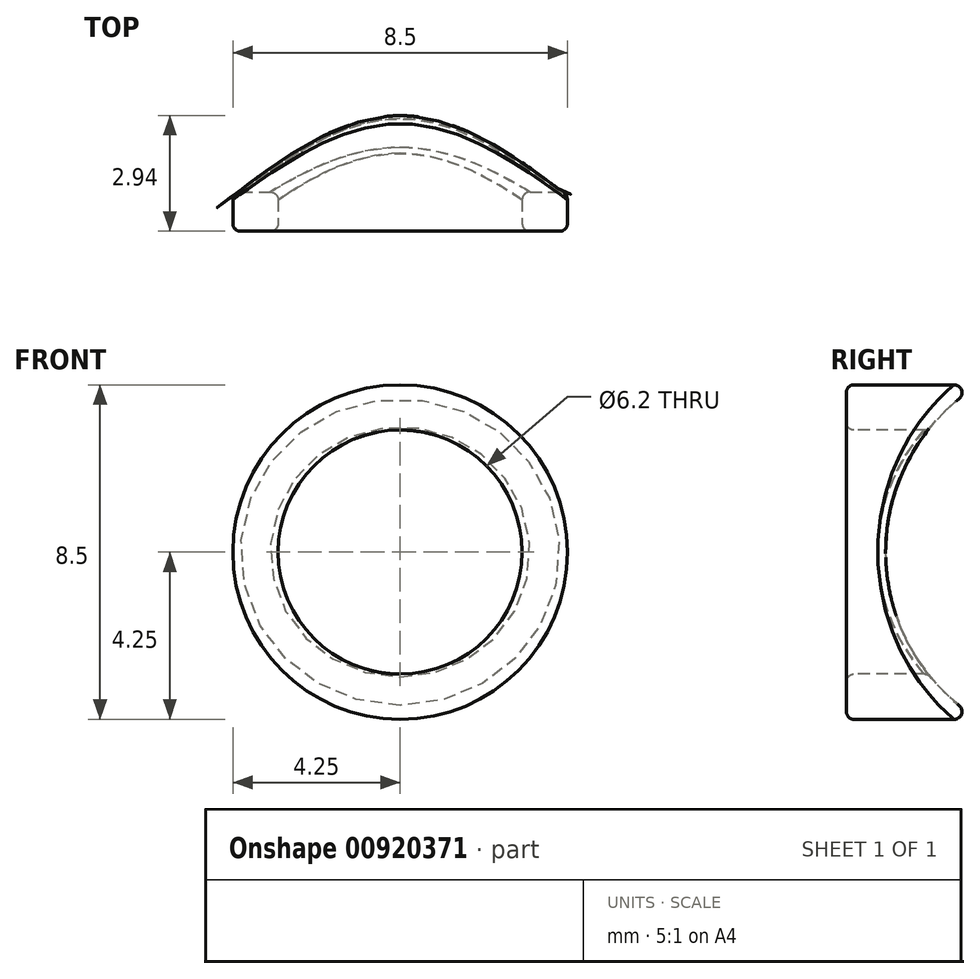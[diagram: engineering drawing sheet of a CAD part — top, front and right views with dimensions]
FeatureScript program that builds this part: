
annotation { "Feature Type Name" : "Feature", "Feature Type Description" : "" }
export const myFeature = defineFeature(function(context is Context, id is Id, definition is map)
    precondition{}
    {
        {
            var Q0;
            Q0=qCreatedBy(makeId("Front.planeOp"),FACE);
            var sketch = newSketch(context, id + "F0", { "sketchPlane" : qUnion([Q0])});
            skCircle(sketch, "E0", {"center": v(0, 0) * mm, "radius": 3.1 * mm});
            skCircle(sketch, "E1", {"center": v(0, 0) * mm, "radius": 4.25 * mm});
            skLineSegment(sketch, "E2", {"start": v(-9, 0) * mm, "end": v(9, 0) * mm, "construction": true});
            skCircle(sketch, "E3", {"center": v(0, 0) * mm, "radius": 9 * mm, "construction": true});
            skLineSegment(sketch, "E4", {"start": v(0, 9) * mm, "end": v(0, -9) * mm, "construction": true});
            skSolve(sketch);
        }
        {
            var Q0;
            Q0 = qSketchRegion(id + "F0", true);
            extrude(context, id + "F1", {"entities" : qUnion([Q0]), "oppositeDirection" : true, "depth" : 5 * mm, "offsetDistance" : 25 * mm});
        }
        {
            var Q0;
            Q0=qCreatedBy(makeId("Right.planeOp"),FACE);
            var sketch = newSketch(context, id + "F2", { "sketchPlane" : qUnion([Q0])});
            skLineSegment(sketch, "E5", {"start": v(0, 0) * mm, "end": v(6, 0) * mm, "construction": true});
            skCircle(sketch, "E6", {"center": v(6, 0) * mm, "radius": 5 * mm});
            skSolve(sketch);
        }
        {
            var Q0;
            Q0 = qSketchRegion(id + "F2", true);
            extrude(context, id + "F3", {"entities" : qUnion([Q0]), "operationType" : NewBodyOperationType.REMOVE, "endBound" : BoundingType.SYMMETRIC, "oppositeDirection" : true, "depth" : 25 * mm, "offsetDistance" : 25 * mm});
        }
        {
            var Q0;
            Q0=makeQuery(id+"F3.boolean.opBoolean","INTERSECT",EDGE,{"derivedFrom":[makeQuery(id+"F1.opExtrude","SWEPT_FACE",FACE,{"disambiguationData":[OSD([sQuery(id+"F0.wireOp",EDGE,"E1")])]}),makeQuery(id+"F3.opExtrude","SWEPT_FACE",FACE,{"disambiguationData":[OSD([sQuery(id+"F2.wireOp",EDGE,"E6")])]})]});
            var Q1;
            Q1=makeQuery(id+"F3.boolean.opBoolean","INTERSECT",EDGE,{"derivedFrom":[makeQuery(id+"F1.opExtrude","SWEPT_FACE",FACE,{"disambiguationData":[OSD([sQuery(id+"F0.wireOp",EDGE,"E0")])]}),makeQuery(id+"F3.opExtrude","SWEPT_FACE",FACE,{"disambiguationData":[OSD([sQuery(id+"F2.wireOp",EDGE,"E6")])]})]});
            var Q2;
            Q2=makeQuery(id+"F1.opExtrude","CAP_EDGE",EDGE,{"disambiguationData":[OSD([sQuery(id+"F0.wireOp",EDGE,"E0")])],"isStart":true});
            var Q3;
            Q3=makeQuery(id+"F1.opExtrude","CAP_EDGE",EDGE,{"disambiguationData":[OSD([sQuery(id+"F0.wireOp",EDGE,"E1")])],"isStart":true});
            fillet(context, id + "F4", {"entities" : qUnion([Q0, Q1, Q2, Q3]), "radius" : .2 * mm, "tangentPropagation" : true, "allowEdgeOverflow" : false});
        }
    });
